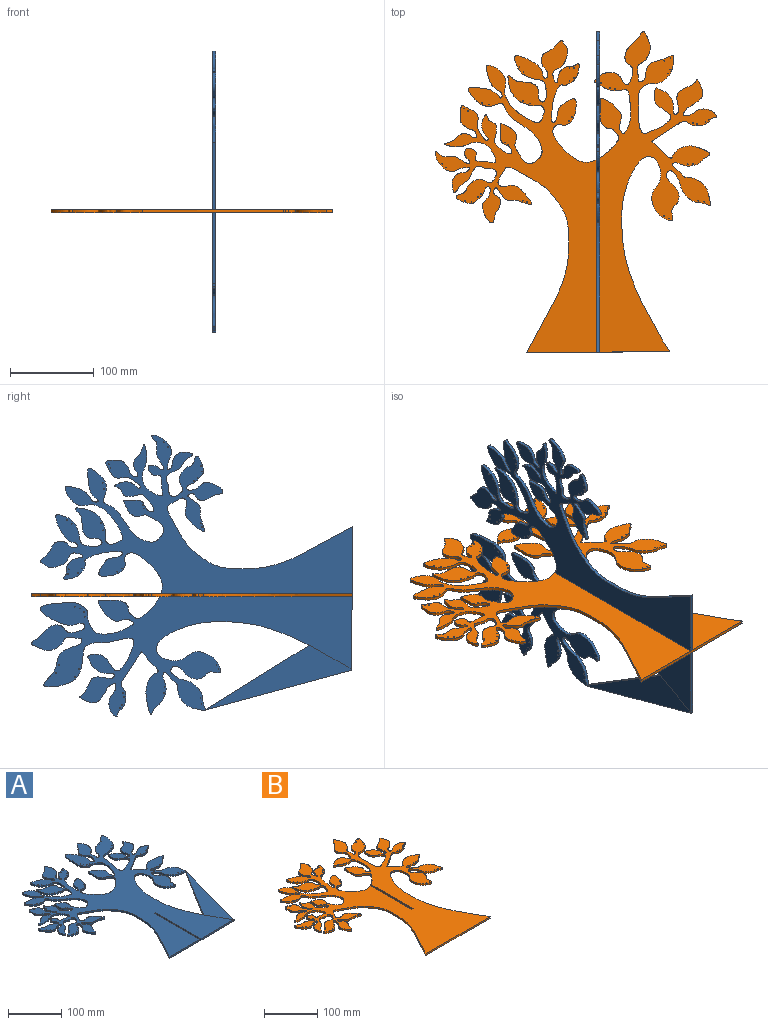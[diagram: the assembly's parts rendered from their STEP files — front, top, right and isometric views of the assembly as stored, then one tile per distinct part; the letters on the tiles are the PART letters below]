
ASSEMBLY  parts=2 mates=1
PART A: 52 faces, bbox 339.3x386.2x3.6 mm
  f0: extruded ~80.61x3.6mm, area 290.2mm2, adj f1,f48,f50,f51
  f1: plane 119.99x3.6mm, normal (1,0,0), area 432mm2, adj f0,f2,f50,f51
  f2: plane 3.6x3.5mm, normal (0,-1,0), area 12.6mm2, adj f1,f3,f50,f51
  f3: plane 119.99x3.6mm, normal (-1,0,0), area 431.9mm2, adj f2,f4,f50,f51
  f4: extruded ~85.02x3.6mm, area 306.1mm2, adj f3,f5,f50,f51
  f5: extruded ~378.37x277.57mm, area 10852.2mm2, adj f4,f6,f50,f51
  f6: extruded ~71.76x62.35mm, area 1274.3mm2, adj f5,f48,f50,f51
  f7: cylinder r=0.5mm len=3.6mm, axis (0,0,-1), area 11.3mm2, adj f50,f51
  f8: cylinder r=0.5mm len=3.6mm, axis (0,0,-1), area 11.3mm2, adj f50,f51
  f9: cylinder r=0.5mm len=3.6mm, axis (0,0,-1), area 11.3mm2, adj f50,f51
  f10: cylinder r=0.5mm len=3.6mm, axis (0,0,-1), area 11.3mm2, adj f50,f51
  f11: cylinder r=0.5mm len=3.6mm, axis (0,0,-1), area 11.3mm2, adj f50,f51
  f12: cylinder r=0.5mm len=3.6mm, axis (0,0,-1), area 11.3mm2, adj f50,f51
  f13: cylinder r=0.5mm len=3.6mm, axis (0,0,-1), area 11.3mm2, adj f50,f51
  f14: cylinder r=0.5mm len=3.6mm, axis (0,0,-1), area 11.3mm2, adj f50,f51
  f15: cylinder r=0.5mm len=3.6mm, axis (0,0,-1), area 11.3mm2, adj f50,f51
  f16: cylinder r=0.5mm len=3.6mm, axis (0,0,-1), area 11.3mm2, adj f50,f51
  f17: cylinder r=0.5mm len=3.6mm, axis (0,0,-1), area 11.3mm2, adj f50,f51
  f18: cylinder r=0.5mm len=3.6mm, axis (0,0,-1), area 11.3mm2, adj f50,f51
  f19: cylinder r=0.5mm len=3.6mm, axis (0,0,-1), area 11.3mm2, adj f50,f51
  f20: cylinder r=0.5mm len=3.6mm, axis (0,0,-1), area 11.3mm2, adj f50,f51
  f21: cylinder r=0.5mm len=3.6mm, axis (0,0,-1), area 11.3mm2, adj f50,f51
  f22: cylinder r=0.5mm len=3.6mm, axis (0,0,-1), area 11.3mm2, adj f50,f51
  f23: cylinder r=0.5mm len=3.6mm, axis (0,0,-1), area 11.3mm2, adj f50,f51
  f24: cylinder r=0.5mm len=3.6mm, axis (0,0,-1), area 11.3mm2, adj f50,f51
  f25: cylinder r=0.5mm len=3.6mm, axis (0,0,-1), area 11.3mm2, adj f50,f51
  f26: cylinder r=0.5mm len=3.6mm, axis (0,0,-1), area 11.3mm2, adj f50,f51
  f27: cylinder r=0.5mm len=3.6mm, axis (0,0,-1), area 11.3mm2, adj f50,f51
  f28: cylinder r=0.5mm len=3.6mm, axis (0,0,-1), area 11.3mm2, adj f50,f51
  f29: cylinder r=0.5mm len=3.6mm, axis (0,0,-1), area 11.3mm2, adj f50,f51
  f30: cylinder r=0.5mm len=3.6mm, axis (0,0,-1), area 11.3mm2, adj f50,f51
  f31: cylinder r=0.5mm len=3.6mm, axis (0,0,-1), area 11.3mm2, adj f50,f51
  f32: cylinder r=0.5mm len=3.6mm, axis (0,0,-1), area 11.3mm2, adj f50,f51
  f33: cylinder r=0.5mm len=3.6mm, axis (0,0,-1), area 11.3mm2, adj f50,f51
  f34: cylinder r=0.5mm len=3.6mm, axis (0,0,-1), area 11.3mm2, adj f50,f51
  f35: cylinder r=0.5mm len=3.6mm, axis (0,0,-1), area 11.3mm2, adj f50,f51
  f36: cylinder r=0.5mm len=3.6mm, axis (0,0,-1), area 11.3mm2, adj f50,f51
  f37: cylinder r=0.5mm len=3.6mm, axis (0,0,-1), area 11.3mm2, adj f50,f51
  f38: cylinder r=0.5mm len=3.6mm, axis (0,0,-1), area 11.3mm2, adj f50,f51
  f39: cylinder r=0.5mm len=3.6mm, axis (0,0,-1), area 11.3mm2, adj f50,f51
  f40: cylinder r=0.5mm len=3.6mm, axis (0,0,-1), area 11.3mm2, adj f50,f51
  f41: cylinder r=0.5mm len=3.6mm, axis (0,0,-1), area 11.3mm2, adj f50,f51
  f42: cylinder r=0.5mm len=3.6mm, axis (0,0,-1), area 11.3mm2, adj f50,f51
  f43: cylinder r=0.5mm len=3.6mm, axis (0,0,-1), area 11.3mm2, adj f50,f51
  f44: cylinder r=0.5mm len=3.6mm, axis (0,0,-1), area 11.3mm2, adj f50,f51
  f45: cylinder r=0.5mm len=3.6mm, axis (0,0,-1), area 11.3mm2, adj f50,f51
  f46: cylinder r=0.5mm len=3.6mm, axis (0,0,-1), area 11.3mm2, adj f50,f51
  f47: cylinder r=0.5mm len=3.6mm, axis (0,0,-1), area 11.3mm2, adj f50,f51
  f48: extruded ~219.07x134.3mm, area 2046.1mm2, adj f0,f6,f50,f51
  f49: cylinder r=0.5mm len=3.6mm, axis (0,0,-1), area 11.3mm2, adj f50,f51
  f50: plane 386.19x339.3mm, normal (0,0,1), area -29400mm2, adj f0,f1,f2,f3,f4,f5,f6,f7
  f51: plane 386.19x339.3mm, normal (0,0,-1), area -29400mm2, adj f0,f1,f2,f3,f4,f5,f6,f7
PART B: 52 faces, bbox 338.7x385.1x3.6 mm
  f0: extruded ~375.7x133.45mm, area 6036.3mm2, adj f1,f48,f50,f51
  f1: plane 112.18x3.6mm, normal (-1,0,0), area 403.9mm2, adj f0,f2,f50,f51
  f2: plane 3.6x3.5mm, normal (0,1,0), area 12.6mm2, adj f1,f3,f50,f51
  f3: plane 110.55x3.6mm, normal (1,0,0), area 398mm2, adj f2,f4,f50,f51
  f4: extruded ~172.97x142.21mm, area 4805.9mm2, adj f3,f5,f50,f51
  f5: extruded ~71.98x62.27mm, area 1276.3mm2, adj f4,f6,f50,f51
  f6: extruded ~219.07x134.3mm, area 2046.1mm2, adj f5,f48,f50,f51
  f7: cylinder r=0.5mm len=3.6mm, axis (0,0,-1), area 11.3mm2, adj f50,f51
  f8: cylinder r=0.5mm len=3.6mm, axis (0,0,-1), area 11.3mm2, adj f50,f51
  f9: cylinder r=0.5mm len=3.6mm, axis (0,0,-1), area 11.3mm2, adj f50,f51
  f10: cylinder r=0.5mm len=3.6mm, axis (0,0,-1), area 11.3mm2, adj f50,f51
  f11: cylinder r=0.5mm len=3.6mm, axis (0,0,-1), area 11.3mm2, adj f50,f51
  f12: cylinder r=0.5mm len=3.6mm, axis (0,0,-1), area 11.3mm2, adj f50,f51
  f13: cylinder r=0.5mm len=3.6mm, axis (0,0,-1), area 11.3mm2, adj f50,f51
  f14: cylinder r=0.5mm len=3.6mm, axis (0,0,-1), area 11.3mm2, adj f50,f51
  f15: cylinder r=0.5mm len=3.6mm, axis (0,0,-1), area 11.3mm2, adj f50,f51
  f16: cylinder r=0.5mm len=3.6mm, axis (0,0,-1), area 11.3mm2, adj f50,f51
  f17: cylinder r=0.5mm len=3.6mm, axis (0,0,-1), area 11.3mm2, adj f50,f51
  f18: cylinder r=0.5mm len=3.6mm, axis (0,0,-1), area 11.3mm2, adj f50,f51
  f19: cylinder r=0.5mm len=3.6mm, axis (0,0,-1), area 11.3mm2, adj f50,f51
  f20: cylinder r=0.5mm len=3.6mm, axis (0,0,-1), area 11.3mm2, adj f50,f51
  f21: cylinder r=0.5mm len=3.6mm, axis (0,0,-1), area 11.3mm2, adj f50,f51
  f22: cylinder r=0.5mm len=3.6mm, axis (0,0,-1), area 11.3mm2, adj f50,f51
  f23: cylinder r=0.5mm len=3.6mm, axis (0,0,-1), area 11.3mm2, adj f50,f51
  f24: cylinder r=0.5mm len=3.6mm, axis (0,0,-1), area 11.3mm2, adj f50,f51
  f25: cylinder r=0.5mm len=3.6mm, axis (0,0,-1), area 11.3mm2, adj f50,f51
  f26: cylinder r=0.5mm len=3.6mm, axis (0,0,-1), area 11.3mm2, adj f50,f51
  f27: cylinder r=0.5mm len=3.6mm, axis (0,0,-1), area 11.3mm2, adj f50,f51
  f28: cylinder r=0.5mm len=3.6mm, axis (0,0,-1), area 11.3mm2, adj f50,f51
  f29: cylinder r=0.5mm len=3.6mm, axis (0,0,-1), area 11.3mm2, adj f50,f51
  f30: cylinder r=0.5mm len=3.6mm, axis (0,0,-1), area 11.3mm2, adj f50,f51
  f31: cylinder r=0.5mm len=3.6mm, axis (0,0,-1), area 11.3mm2, adj f50,f51
  f32: cylinder r=0.5mm len=3.6mm, axis (0,0,-1), area 11.3mm2, adj f50,f51
  f33: cylinder r=0.5mm len=3.6mm, axis (0,0,-1), area 11.3mm2, adj f50,f51
  f34: cylinder r=0.5mm len=3.6mm, axis (0,0,-1), area 11.3mm2, adj f50,f51
  f35: cylinder r=0.5mm len=3.6mm, axis (0,0,-1), area 11.3mm2, adj f50,f51
  f36: cylinder r=0.5mm len=3.6mm, axis (0,0,-1), area 11.3mm2, adj f50,f51
  f37: cylinder r=0.5mm len=3.6mm, axis (0,0,-1), area 11.3mm2, adj f50,f51
  f38: cylinder r=0.5mm len=3.6mm, axis (0,0,-1), area 11.3mm2, adj f50,f51
  f39: cylinder r=0.5mm len=3.6mm, axis (0,0,-1), area 11.3mm2, adj f50,f51
  f40: cylinder r=0.5mm len=3.6mm, axis (0,0,-1), area 11.3mm2, adj f50,f51
  f41: cylinder r=0.5mm len=3.6mm, axis (0,0,-1), area 11.3mm2, adj f50,f51
  f42: cylinder r=0.5mm len=3.6mm, axis (0,0,-1), area 11.3mm2, adj f50,f51
  f43: cylinder r=0.5mm len=3.6mm, axis (0,0,-1), area 11.3mm2, adj f50,f51
  f44: cylinder r=0.5mm len=3.6mm, axis (0,0,-1), area 11.3mm2, adj f50,f51
  f45: cylinder r=0.5mm len=3.6mm, axis (0,0,-1), area 11.3mm2, adj f50,f51
  f46: cylinder r=0.5mm len=3.6mm, axis (0,0,-1), area 11.3mm2, adj f50,f51
  f47: cylinder r=0.5mm len=3.6mm, axis (0,0,-1), area 11.3mm2, adj f50,f51
  f48: extruded ~168.98x3.6mm, area 608.3mm2, adj f0,f6,f50,f51
  f49: cylinder r=0.5mm len=3.6mm, axis (0,0,-1), area 11.3mm2, adj f50,f51
  f50: plane 385.13x338.68mm, normal (0,0,1), area 58135.7mm2, adj f0,f1,f2,f3,f4,f5,f6,f7
  f51: plane 385.13x338.68mm, normal (0,0,-1), area 58135.7mm2, adj f0,f1,f2,f3,f4,f5,f6,f7
PLACE A rot(axis=(0,1,0),90deg) t=(-119.99,-181.11,5.86)mm
PLACE B t=(31.01,-181.11,156.41)mm
MATE fastened A.f2 <-> B.f2  axis (0,-1,0) through (-118.19,-51.63,158.21)mm
